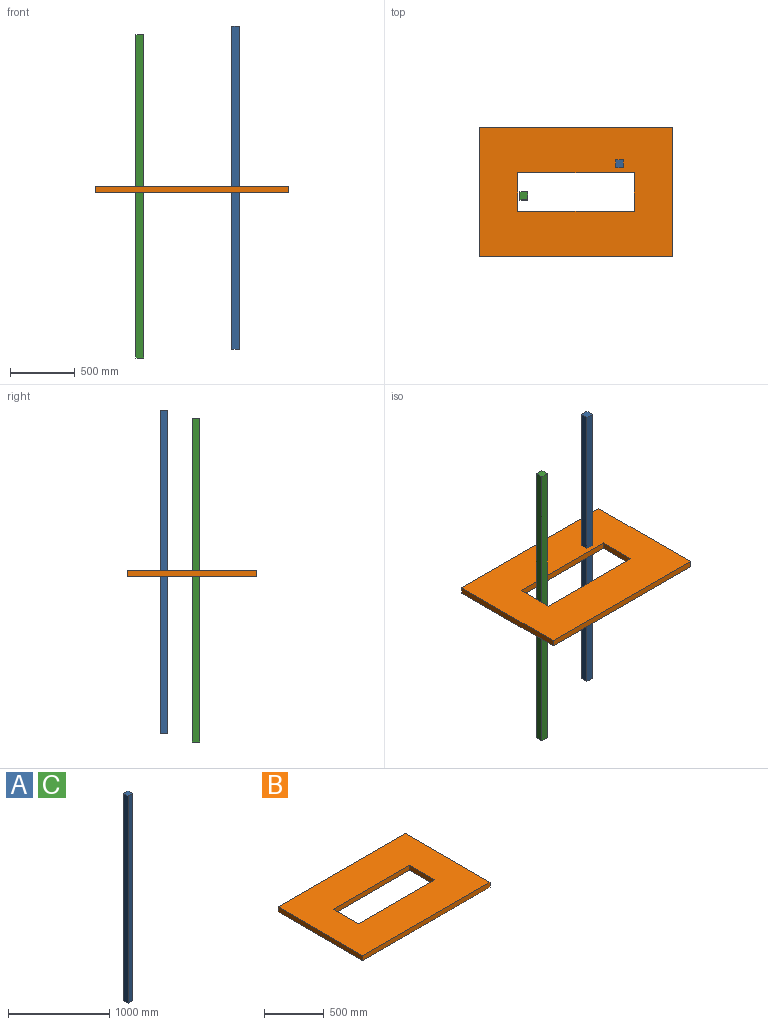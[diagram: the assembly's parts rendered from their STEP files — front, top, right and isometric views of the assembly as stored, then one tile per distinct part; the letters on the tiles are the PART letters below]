
ASSEMBLY  parts=3 mates=2
PART A: 6 faces, bbox 60x60x2500 mm
  f0: plane 2500x60mm, normal (0,1,0), area 150000mm2, adj f1,f3,f4,f5
  f1: plane 2500x60mm, normal (-1,0,0), area 150000mm2, adj f0,f2,f4,f5
  f2: plane 2500x60mm, normal (0,-1,0), area 150000mm2, adj f1,f3,f4,f5
  f3: plane 2500x60mm, normal (1,0,0), area 150000mm2, adj f0,f2,f4,f5
  f4: plane 60x60mm, normal (0,0,1), area 3600mm2, adj f0,f1,f2,f3
  f5: plane 60x60mm, normal (0,0,-1), area 3600mm2, adj f0,f1,f2,f3
PART B: 10 faces, bbox 1500x1000x50 mm
  f0: plane 1500x50mm, normal (0,1,0), area 75000mm2, adj f1,f7,f8,f9
  f1: plane 1000x50mm, normal (-1,0,0), area 50000mm2, adj f0,f2,f8,f9
  f2: plane 1500x50mm, normal (0,-1,0), area 75000mm2, adj f1,f7,f8,f9
  f3: plane 300x50mm, normal (1,0,0), area 15000mm2, adj f4,f6,f8,f9
  f4: plane 900x50mm, normal (0,-1,0), area 45000mm2, adj f3,f5,f8,f9
  f5: plane 300x50mm, normal (-1,0,0), area 15000mm2, adj f4,f6,f8,f9
  f6: plane 900x50mm, normal (0,1,0), area 45000mm2, adj f3,f5,f8,f9
  f7: plane 1000x50mm, normal (1,0,0), area 50000mm2, adj f0,f2,f8,f9
  f8: plane 1500x1000mm, normal (0,0,1), area 1230000mm2, adj f0,f1,f2,f3,f4,f5,f6,f7
  f9: plane 1500x1000mm, normal (0,0,-1), area 1230000mm2, adj f0,f1,f2,f3,f4,f5,f6,f7
PART C: same geometry as A
PLACE A t=(291.56,205.78,-1193.82)mm
PLACE B t=(-45.42,-11.28,15.37)mm
PLACE C t=(-449.11,-41.58,-1261.61)mm
MATE parallel C.f0 <-> B.f4  axis (0,1,0) through (-449.11,-11.58,-11.61)mm
MATE parallel C.f1 <-> B.f3  axis (-1,0,0) through (-479.11,-41.58,-11.61)mm
